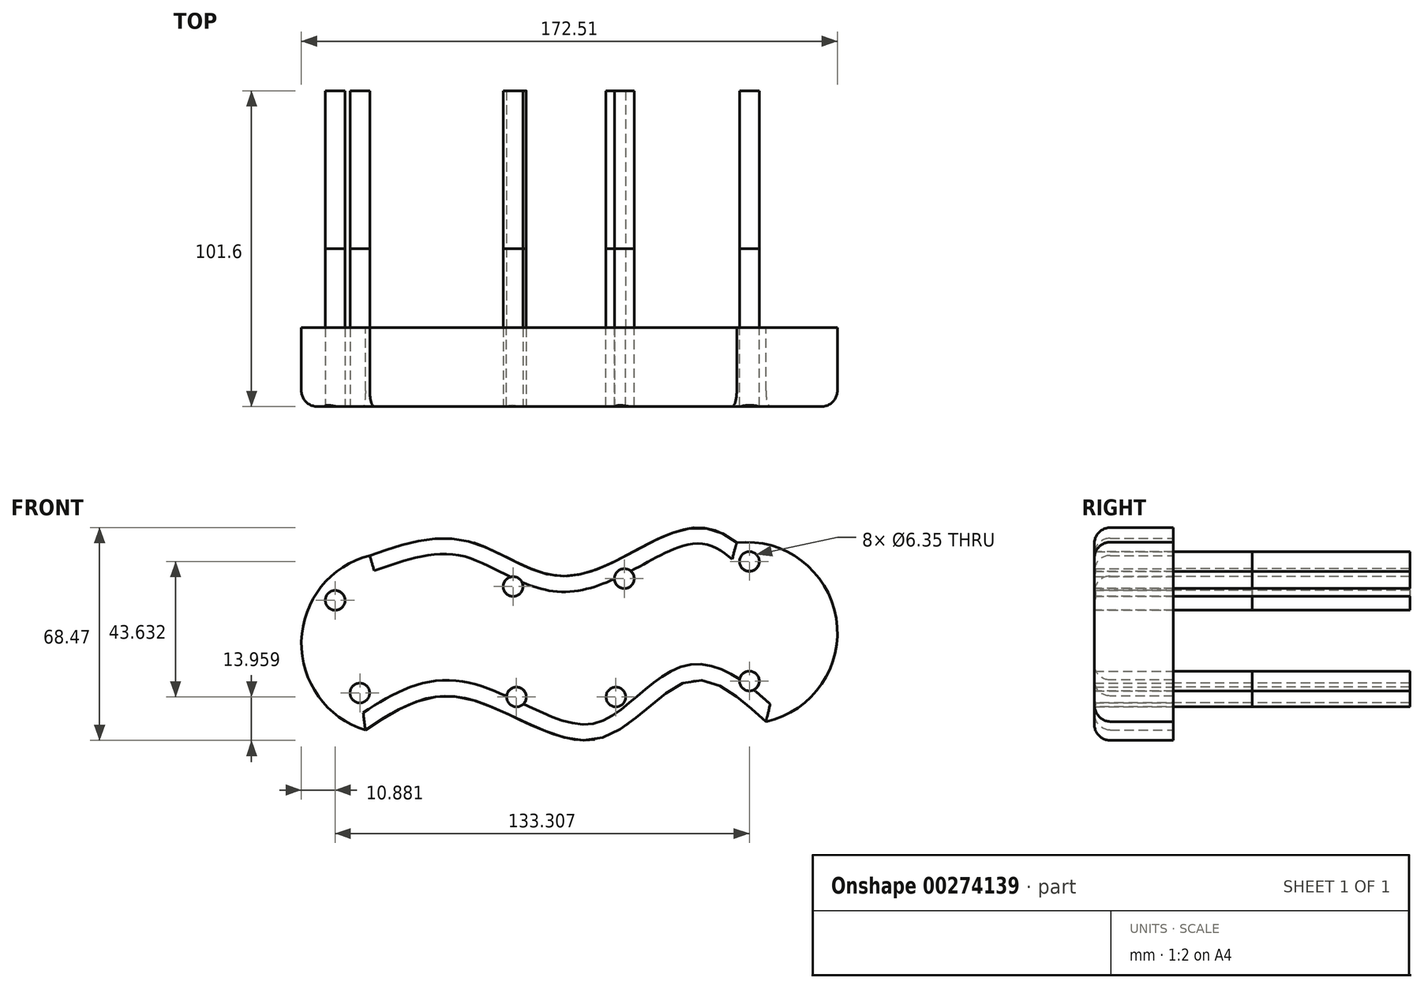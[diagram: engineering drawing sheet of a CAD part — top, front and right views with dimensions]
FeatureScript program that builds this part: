
annotation { "Feature Type Name" : "Feature", "Feature Type Description" : "" }
export const myFeature = defineFeature(function(context is Context, id is Id, definition is map)
    precondition{}
    {
        {
            var Q0;
            Q0=qCreatedBy(makeId("Front.planeOp"),FACE);
            var sketch = newSketch(context, id + "F0", { "sketchPlane" : qUnion([Q0])});
            skArc(sketch, "E0", {"start": v(-56.75, 65.54) * mm, "mid": v(-78.73, 37.96) * mm, "end": v(-58.14, 9.33) * mm});
            skFitSpline(sketch, "E1", {"points": [v(-56.75, 65.54) * mm, v(-25.46, 70.25) * mm, v(5, 58.9) * mm, v(37.12, 71.36) * mm, v(61.37, 69.66) * mm], "startDerivative": vector(128.8, 44.76) * mm, "endDerivative": vector(113.83, -91.35) * mm});
            skArc(sketch, "E2", {"start": v(70.77, 12.08) * mm, "mid": v(93.39, 45.33) * mm, "end": v(61.37, 69.66) * mm});
            skFitSpline(sketch, "E3", {"points": [v(-58.14, 9.33) * mm, v(-27.7, 19.99) * mm, v(15.7, 6.28) * mm, v(45.98, 25.13) * mm, v(70.77, 12.08) * mm], "startDerivative": vector(118.58, 78.49) * mm, "endDerivative": vector(111.15, -101.37) * mm});
            skCircle(sketch, "E4", {"center": v(-59.93, 21.28) * mm, "radius": 3.18 * mm});
            skCircle(sketch, "E5", {"center": v(-9.5, 19.99) * mm, "radius": 3.18 * mm});
            skCircle(sketch, "E6", {"center": v(22.5, 19.99) * mm, "radius": 3.18 * mm});
            skCircle(sketch, "E7", {"center": v(65.45, 25.13) * mm, "radius": 3.18 * mm});
            skCircle(sketch, "E8", {"center": v(65.45, 63.62) * mm, "radius": 3.18 * mm});
            skCircle(sketch, "E9", {"center": v(25.2, 58.09) * mm, "radius": 3.18 * mm});
            skCircle(sketch, "E10", {"center": v(-10.6, 55.54) * mm, "radius": 3.18 * mm});
            skCircle(sketch, "E11", {"center": v(-67.86, 51.09) * mm, "radius": 3.18 * mm});
            skSolve(sketch);
        }
        {
            var Q0;
            Q0 = qSketchRegion(id + "F0", true);
            extrude(context, id + "F1", {"entities" : qUnion([Q0]), "depth" : 25.4 * mm});
        }
        {
            var Q0;
            Q0=makeQuery(id+"F0.imprint","IMPRINT",FACE,{"disambiguationData":[TD([[makeQuery(id+"F0.imprint","IMPRINT",EDGE,{"derivedFrom":sQuery(id+"F0.wireOp",EDGE,"E4")}),1.0]])]});
            var Q1;
            Q1=makeQuery(id+"F0.imprint","IMPRINT",FACE,{"disambiguationData":[TD([[makeQuery(id+"F0.imprint","IMPRINT",EDGE,{"derivedFrom":sQuery(id+"F0.wireOp",EDGE,"E11")}),1.0]])]});
            var Q2;
            Q2=makeQuery(id+"F0.imprint","IMPRINT",FACE,{"disambiguationData":[TD([[makeQuery(id+"F0.imprint","IMPRINT",EDGE,{"derivedFrom":sQuery(id+"F0.wireOp",EDGE,"E10")}),1.0]])]});
            var Q3;
            Q3=makeQuery(id+"F0.imprint","IMPRINT",FACE,{"disambiguationData":[TD([[makeQuery(id+"F0.imprint","IMPRINT",EDGE,{"derivedFrom":sQuery(id+"F0.wireOp",EDGE,"E5")}),1.0]])]});
            var Q4;
            Q4=makeQuery(id+"F0.imprint","IMPRINT",FACE,{"disambiguationData":[TD([[makeQuery(id+"F0.imprint","IMPRINT",EDGE,{"derivedFrom":sQuery(id+"F0.wireOp",EDGE,"E6")}),1.0]])]});
            var Q5;
            Q5=makeQuery(id+"F0.imprint","IMPRINT",FACE,{"disambiguationData":[TD([[makeQuery(id+"F0.imprint","IMPRINT",EDGE,{"derivedFrom":sQuery(id+"F0.wireOp",EDGE,"E9")}),1.0]])]});
            var Q6;
            Q6=makeQuery(id+"F0.imprint","IMPRINT",FACE,{"disambiguationData":[TD([[makeQuery(id+"F0.imprint","IMPRINT",EDGE,{"derivedFrom":sQuery(id+"F0.wireOp",EDGE,"E8")}),1.0]])]});
            var Q7;
            Q7=makeQuery(id+"F0.imprint","IMPRINT",FACE,{"disambiguationData":[TD([[makeQuery(id+"F0.imprint","IMPRINT",EDGE,{"derivedFrom":sQuery(id+"F0.wireOp",EDGE,"E7")}),1.0]])]});
            extrude(context, id + "F2", {"entities" : qUnion([Q0, Q1, Q2, Q3, Q4, Q5, Q6, Q7]), "oppositeDirection" : true, "depth" : 76.2 * mm});
        }
        {
            var Q0;
            Q0=makeQuery(id+"F1.opExtrude","CAP_EDGE",EDGE,{"disambiguationData":[OSD([sQuery(id+"F0.wireOp",EDGE,"E0")])],"isStart":false});
            var Q1;
            Q1=makeQuery(id+"F1.opExtrude","CAP_EDGE",EDGE,{"disambiguationData":[OSD([sQuery(id+"F0.wireOp",EDGE,"E3")])],"isStart":false});
            var Q2;
            Q2=makeQuery(id+"F1.opExtrude","CAP_EDGE",EDGE,{"disambiguationData":[OSD([sQuery(id+"F0.wireOp",EDGE,"E2")])],"isStart":false});
            var Q3;
            Q3=makeQuery(id+"F1.opExtrude","CAP_EDGE",EDGE,{"disambiguationData":[OSD([sQuery(id+"F0.wireOp",EDGE,"E1")])],"isStart":false});
            fillet(context, id + "F3", {"entities" : qUnion([Q0, Q1, Q2, Q3]), "radius" : 5.08 * mm, "tangentPropagation" : true, "allowEdgeOverflow" : false});
        }
        {
            var Q0;
            Q0=makeQuery(id+"F0.imprint","IMPRINT",FACE,{"disambiguationData":[TD([[makeQuery(id+"F0.imprint","IMPRINT",EDGE,{"derivedFrom":sQuery(id+"F0.wireOp",EDGE,"E4")}),1.0]])]});
            var Q1;
            Q1=makeQuery(id+"F0.imprint","IMPRINT",FACE,{"disambiguationData":[TD([[makeQuery(id+"F0.imprint","IMPRINT",EDGE,{"derivedFrom":sQuery(id+"F0.wireOp",EDGE,"E11")}),1.0]])]});
            var Q2;
            Q2=makeQuery(id+"F0.imprint","IMPRINT",FACE,{"disambiguationData":[TD([[makeQuery(id+"F0.imprint","IMPRINT",EDGE,{"derivedFrom":sQuery(id+"F0.wireOp",EDGE,"E10")}),1.0]])]});
            var Q3;
            Q3=makeQuery(id+"F0.imprint","IMPRINT",FACE,{"disambiguationData":[TD([[makeQuery(id+"F0.imprint","IMPRINT",EDGE,{"derivedFrom":sQuery(id+"F0.wireOp",EDGE,"E9")}),1.0]])]});
            var Q4;
            Q4=makeQuery(id+"F0.imprint","IMPRINT",FACE,{"disambiguationData":[TD([[makeQuery(id+"F0.imprint","IMPRINT",EDGE,{"derivedFrom":sQuery(id+"F0.wireOp",EDGE,"E6")}),1.0]])]});
            var Q5;
            Q5=makeQuery(id+"F0.imprint","IMPRINT",FACE,{"disambiguationData":[TD([[makeQuery(id+"F0.imprint","IMPRINT",EDGE,{"derivedFrom":sQuery(id+"F0.wireOp",EDGE,"E5")}),1.0]])]});
            var Q6;
            Q6=makeQuery(id+"F0.imprint","IMPRINT",FACE,{"disambiguationData":[TD([[makeQuery(id+"F0.imprint","IMPRINT",EDGE,{"derivedFrom":sQuery(id+"F0.wireOp",EDGE,"E8")}),1.0]])]});
            var Q7;
            Q7=makeQuery(id+"F0.imprint","IMPRINT",FACE,{"disambiguationData":[TD([[makeQuery(id+"F0.imprint","IMPRINT",EDGE,{"derivedFrom":sQuery(id+"F0.wireOp",EDGE,"E7")}),1.0]])]});
            extrude(context, id + "F4", {"entities" : qUnion([Q0, Q1, Q2, Q3, Q4, Q5, Q6, Q7]), "endBound" : BoundingType.SYMMETRIC, "oppositeDirection" : true, "depth" : 50.8 * mm});
        }
    });
